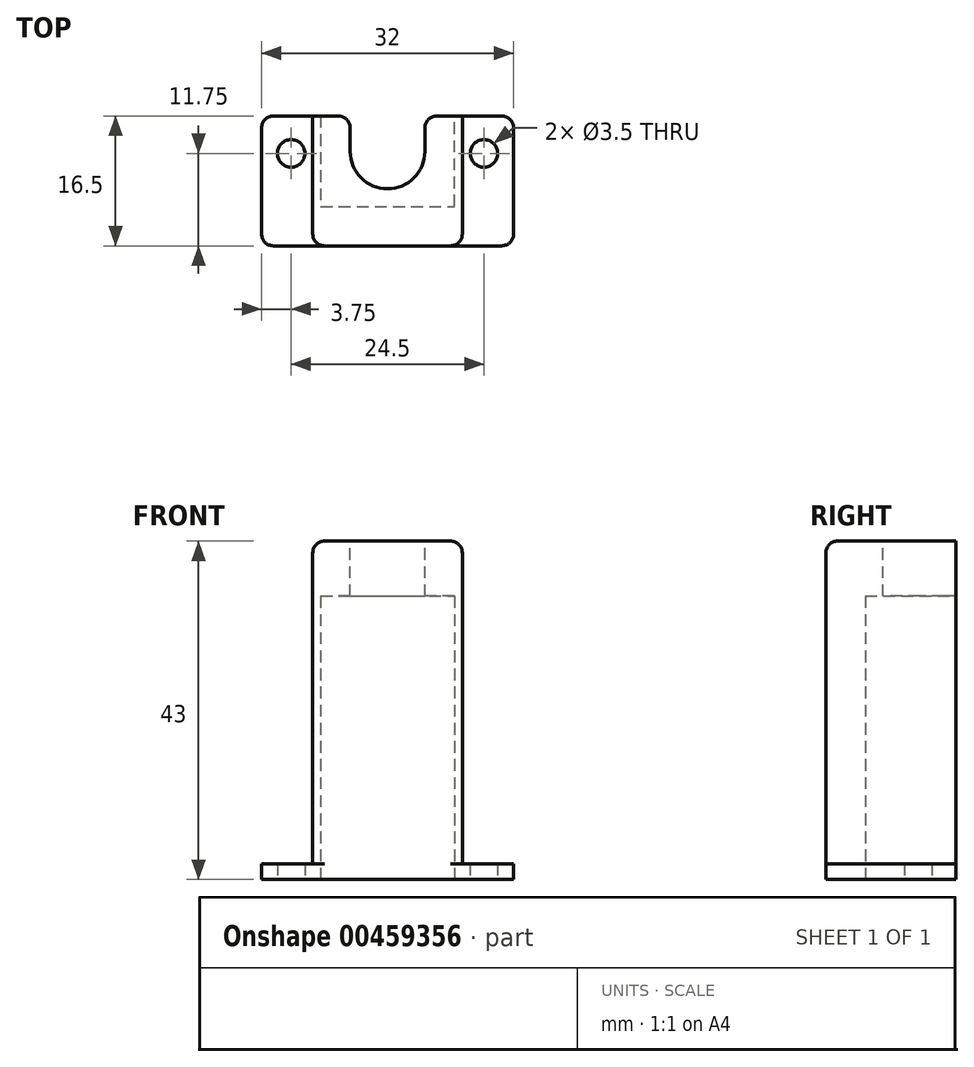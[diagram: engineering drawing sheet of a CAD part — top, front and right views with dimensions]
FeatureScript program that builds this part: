
annotation { "Feature Type Name" : "Feature", "Feature Type Description" : "" }
export const myFeature = defineFeature(function(context is Context, id is Id, definition is map)
    precondition{}
    {
        {
            var Q0;
            Q0=qCreatedBy(makeId("Top.planeOp"),FACE);
            var sketch = newSketch(context, id + "F0", { "sketchPlane" : qUnion([Q0])});
            skLineSegment(sketch, "E0.top", {"start": v(0, -16.5) * mm, "end": v(32, -16.5) * mm});
            skLineSegment(sketch, "E0.left", {"start": v(0, 0) * mm, "end": v(0, -16.5) * mm});
            skLineSegment(sketch, "E0.right", {"start": v(32, 0) * mm, "end": v(32, -16.5) * mm});
            skCircle(sketch, "E1", {"center": v(3.75, -4.75) * mm, "radius": 1.75 * mm});
            skCircle(sketch, "E2", {"center": v(28.25, -4.75) * mm, "radius": 1.75 * mm});
            skLineSegment(sketch, "E3", {"start": v(7.5, 0) * mm, "end": v(7.5, -11.5) * mm});
            skLineSegment(sketch, "E4", {"start": v(7.5, -11.5) * mm, "end": v(24.5, -11.5) * mm});
            skLineSegment(sketch, "E5", {"start": v(24.5, -11.5) * mm, "end": v(24.5, 0) * mm});
            skLineSegment(sketch, "E6", {"start": v(24.5, 0) * mm, "end": v(32, 0) * mm});
            skLineSegment(sketch, "E7", {"start": v(7.5, 0) * mm, "end": v(0, 0) * mm});
            skLineSegment(sketch, "E8", {"start": v(16, -11.5) * mm, "end": v(16, 0) * mm, "construction": true});
            skLineSegment(sketch, "E9", {"start": v(3.75, -4.75) * mm, "end": v(28.25, -4.75) * mm, "construction": true});
            skPoint(sketch, "E10", {"position": v(16, -4.75) * mm});
            skSolve(sketch);
        }
        {
            var Q0;
            Q0 = qSketchRegion(id + "F0", true);
            extrude(context, id + "F1", {"entities" : qUnion([Q0]), "depth" : 2 * mm});
        }
        {
            var Q0;
            Q0=makeQuery(id+"F1.opExtrude","CAP_FACE",FACE,{"disambiguationData":[OSD([sQuery(id+"F0.wireOp",EDGE,"E0.top"),sQuery(id+"F0.wireOp",EDGE,"E0.left"),sQuery(id+"F0.wireOp",EDGE,"E0.right"),sQuery(id+"F0.wireOp",EDGE,"E1"),sQuery(id+"F0.wireOp",EDGE,"E2"),sQuery(id+"F0.wireOp",EDGE,"E3"),sQuery(id+"F0.wireOp",EDGE,"E4"),sQuery(id+"F0.wireOp",EDGE,"E5"),sQuery(id+"F0.wireOp",EDGE,"E6"),sQuery(id+"F0.wireOp",EDGE,"E7")])],"isStart":false});
            var sketch = newSketch(context, id + "F2", { "sketchPlane" : qUnion([Q0])});
            skLineSegment(sketch, "E11", {"start": v(7.5, 0) * mm, "end": v(7.5, -11.5) * mm});
            skLineSegment(sketch, "E12", {"start": v(7.5, -11.5) * mm, "end": v(24.5, -11.5) * mm});
            skLineSegment(sketch, "E13", {"start": v(24.5, -11.5) * mm, "end": v(24.5, 0) * mm});
            skLineSegment(sketch, "E14", {"start": v(24.5, 0) * mm, "end": v(25.5, 0) * mm});
            skLineSegment(sketch, "E15", {"start": v(25.5, 0) * mm, "end": v(25.5, -16.5) * mm});
            skLineSegment(sketch, "E16", {"start": v(25.5, -16.5) * mm, "end": v(6.5, -16.5) * mm});
            skLineSegment(sketch, "E17", {"start": v(6.5, -16.5) * mm, "end": v(6.5, 0) * mm});
            skLineSegment(sketch, "E18", {"start": v(6.5, 0) * mm, "end": v(7.5, 0) * mm});
            skSolve(sketch);
        }
        {
            var Q0;
            Q0 = qSketchRegion(id + "F2", true);
            extrude(context, id + "F3", {"entities" : qUnion([Q0]), "operationType" : NewBodyOperationType.ADD, "depth" : (43 - 2) * mm});
        }
        {
            var Q0;
            Q0=makeQuery(id+"F3.opExtrude","CAP_FACE",FACE,{"disambiguationData":[OSD([sQuery(id+"F2.wireOp",EDGE,"E11"),sQuery(id+"F2.wireOp",EDGE,"E12"),sQuery(id+"F2.wireOp",EDGE,"E13"),sQuery(id+"F2.wireOp",EDGE,"E14"),sQuery(id+"F2.wireOp",EDGE,"E15"),sQuery(id+"F2.wireOp",EDGE,"E16"),sQuery(id+"F2.wireOp",EDGE,"E17"),sQuery(id+"F2.wireOp",EDGE,"E18")])],"isStart":false});
            var sketch = newSketch(context, id + "F4", { "sketchPlane" : qUnion([Q0])});
            skCircle(sketch, "E19", {"center": v(16, -4.5) * mm, "radius": 4.75 * mm});
            skLineSegment(sketch, "E20", {"start": v(16, -11.5) * mm, "end": v(16, 2.5) * mm, "construction": true});
            skLineSegment(sketch, "E21", {"start": v(7.5, 0) * mm, "end": v(11.25, 0) * mm});
            skLineSegment(sketch, "E22", {"start": v(11.25, 0) * mm, "end": v(11.25, -4.5) * mm});
            skLineSegment(sketch, "E23", {"start": v(24.5, 0) * mm, "end": v(20.75, 0) * mm});
            skLineSegment(sketch, "E24", {"start": v(20.75, 0) * mm, "end": v(20.75, -4.5) * mm});
            skSolve(sketch);
        }
        {
            var Q0;
            Q0=makeQuery(id+"F4.imprint","IMPRINT",FACE,{"disambiguationData":[TD([[makeQuery(id+"F4.imprint","IMPRINT",EDGE,{"derivedFrom":sQuery(id+"F4.wireOp",EDGE,"E21")}),-1.0]])]});
            extrude(context, id + "F5", {"entities" : qUnion([Q0]), "operationType" : NewBodyOperationType.ADD, "oppositeDirection" : true, "depth" : 7 * mm});
        }
        {
            var Q0;
            Q0=makeQuery(id+"F3.opExtrude","CAP_EDGE",EDGE,{"disambiguationData":[OSD([sQuery(id+"F2.wireOp",EDGE,"E15")])],"isStart":false});
            var Q1;
            Q1=makeQuery(id+"F5.opExtrude","SWEPT_EDGE",EDGE,{"disambiguationData":[OSD([sQuery(id+"F4.wireOp",EDGE,"E21"),sQuery(id+"F4.wireOp",EDGE,"E22")])]});
            var Q2;
            Q2=makeQuery(id+"F5.opExtrude","SWEPT_EDGE",EDGE,{"disambiguationData":[OSD([sQuery(id+"F4.wireOp",EDGE,"E23"),sQuery(id+"F4.wireOp",EDGE,"E24")])]});
            var Q3;
            Q3=makeQuery(id+"F3.opExtrude","CAP_EDGE",EDGE,{"disambiguationData":[OSD([sQuery(id+"F2.wireOp",EDGE,"E17")])],"isStart":false});
            var Q4;
            Q4=makeQuery(id+"F3.opExtrude","SWEPT_EDGE",EDGE,{"disambiguationData":[OSD([sQuery(id+"F0.wireOp",EDGE,"E0.top"),sQuery(id+"F2.wireOp",EDGE,"E16"),sQuery(id+"F2.wireOp",EDGE,"E17")])]});
            var Q5;
            Q5=makeQuery(id+"F3.opExtrude","CAP_EDGE",EDGE,{"disambiguationData":[OSD([sQuery(id+"F2.wireOp",EDGE,"E16")])],"isStart":false});
            var Q6;
            Q6=makeQuery(id+"F3.opExtrude","SWEPT_EDGE",EDGE,{"disambiguationData":[OSD([sQuery(id+"F0.wireOp",EDGE,"E0.top"),sQuery(id+"F2.wireOp",EDGE,"E15"),sQuery(id+"F2.wireOp",EDGE,"E16")])]});
            var Q7;
            Q7=makeQuery(id+"F1.opExtrude","SWEPT_EDGE",EDGE,{"disambiguationData":[OSD([sQuery(id+"F0.wireOp",EDGE,"E0.top"),sQuery(id+"F0.wireOp",EDGE,"E0.right")])]});
            var Q8;
            Q8=makeQuery(id+"F1.opExtrude","SWEPT_EDGE",EDGE,{"disambiguationData":[OSD([sQuery(id+"F0.wireOp",EDGE,"E0.right"),sQuery(id+"F0.wireOp",EDGE,"E6")])]});
            var Q9;
            Q9=makeQuery(id+"F1.opExtrude","SWEPT_EDGE",EDGE,{"disambiguationData":[OSD([sQuery(id+"F0.wireOp",EDGE,"E0.top"),sQuery(id+"F0.wireOp",EDGE,"E0.left")])]});
            var Q10;
            Q10=makeQuery(id+"F1.opExtrude","SWEPT_EDGE",EDGE,{"disambiguationData":[OSD([sQuery(id+"F0.wireOp",EDGE,"E0.left"),sQuery(id+"F0.wireOp",EDGE,"E7")])]});
            fillet(context, id + "F6", {"entities" : qUnion([Q0, Q1, Q2, Q3, Q4, Q5, Q6, Q7, Q8, Q9, Q10]), "radius" : 1.5 * mm, "tangentPropagation" : true, "allowEdgeOverflow" : false});
        }
    });
